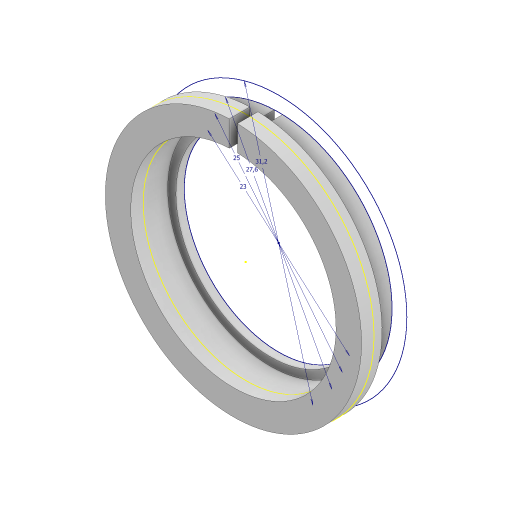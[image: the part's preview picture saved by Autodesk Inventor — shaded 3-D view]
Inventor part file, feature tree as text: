
AUTODESK INVENTOR PART (.ipt)
format: ipt  version: 2023 (Build 270158000, 158)  size: 165,376 bytes
history: native  units: mm
features: extrude x5, sketch x3
ambient origin geometry x8: Origin, YZ Plane, XZ Plane, XY Plane, X Axis, Y Axis, Z Axis, Center Point
bodies: Solid1 (feature_tree)
feature tree (8):
  sketch  "Sketch1"  dims[d0=27.6mm d1=23.0mm]
  extrude  "Extrusion1"  Depth=23.0mm
  extrude  "Extrusion2"  Depth=25.0mm
  sketch  "Sketch2"  dims[d2=31.2mm d3=25.0mm]
  extrude  "Extrusion3"  Depth=4.0mm TaperAngle=0.0deg
  extrude  "Extrusion5"  Depth=1.0mm TaperAngle=0.0deg
  extrude  "Extrusion4"  Depth=1.0mm
  sketch  "Sketch3"  dims[d4=1.0mm d5=0.0mm d6=4.0mm d7=0.0mm d8=1.5mm d9=0.0mm d10=1.0mm d11=8.0mm d12=10.0mm d13=0.0mm d14=1.0mm d15=0.0mm d16=0.5mm d17=0.872665mm d18=0.5mm d19=0.872665mm]
